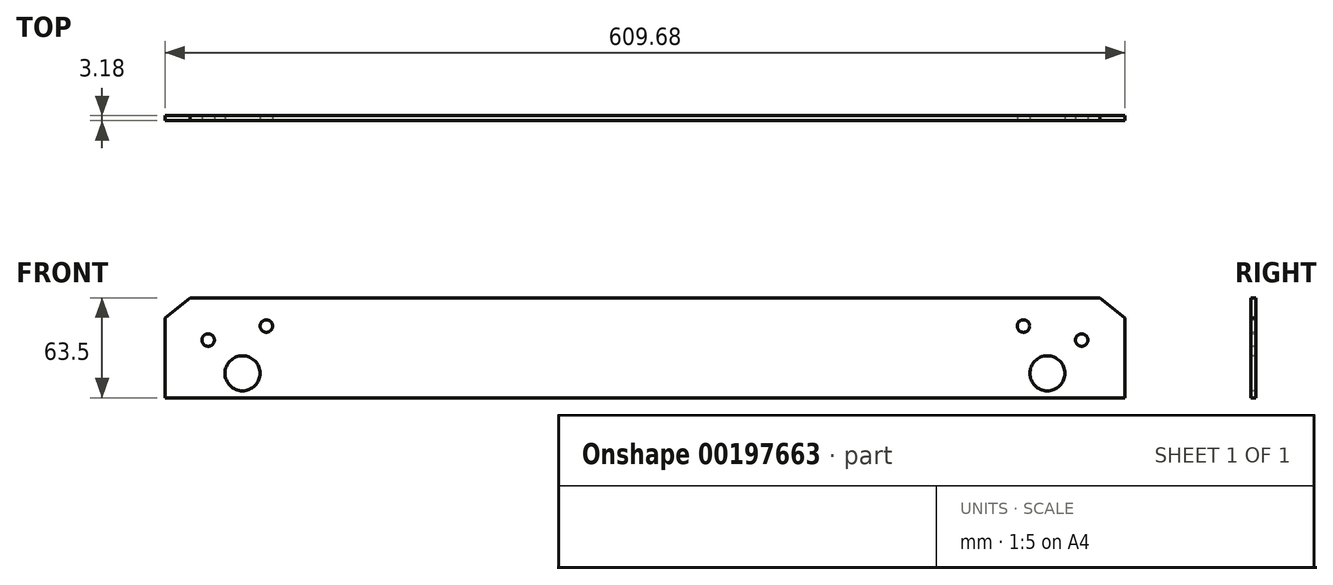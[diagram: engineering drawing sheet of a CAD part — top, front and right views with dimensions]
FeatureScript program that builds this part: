
annotation { "Feature Type Name" : "Feature", "Feature Type Description" : "" }
export const myFeature = defineFeature(function(context is Context, id is Id, definition is map)
    precondition{}
    {
        {
            var Q0;
            Q0=qCreatedBy(makeId("Front.planeOp"),FACE);
            var sketch = newSketch(context, id + "F0", { "sketchPlane" : qUnion([Q0])});
            skLineSegment(sketch, "E0.0", {"start": v(-467.1, 51.6) * mm, "end": v(110.76, 51.6) * mm});
            skCircle(sketch, "E1", {"center": v(99.23, 24.79) * mm, "radius": 3.96 * mm});
            skCircle(sketch, "E2", {"center": v(62.27, 33.68) * mm, "radius": 3.96 * mm});
            skCircle(sketch, "E3", {"center": v(77.43, 3.65) * mm, "radius": 11.11 * mm});
            skLineSegment(sketch, "E4.0", {"start": v(126.73, 38.9) * mm, "end": v(126.65, -11.9) * mm});
            skLineSegment(sketch, "E5.0", {"start": v(-482.87, 38.9) * mm, "end": v(-482.95, -11.9) * mm});
            skCircle(sketch, "E6.MirrorC", {"center": v(-455.56, 24.79) * mm, "radius": 3.96 * mm});
            skCircle(sketch, "E7.MirrorC", {"center": v(-418.6, 33.68) * mm, "radius": 3.96 * mm});
            skCircle(sketch, "E8.MirrorC", {"center": v(-433.77, 3.65) * mm, "radius": 11.11 * mm});
            skLineSegment(sketch, "E9", {"start": v(110.76, 51.6) * mm, "end": v(126.73, 38.9) * mm});
            skLineSegment(sketch, "E10", {"start": v(-467.1, 51.6) * mm, "end": v(-482.79, 38.9) * mm});
            skLineSegment(sketch, "E11", {"start": v(126.65, -11.9) * mm, "end": v(-482.95, -11.9) * mm});
            skSolve(sketch);
        }
        {
            var Q0;
            Q0=sQuery(id+"F0.wireOp",EDGE,"E0.0");
            var Q1;
            Q1=sQuery(id+"F0.wireOp",EDGE,"02333bd6-0d12-4fb4-9101-4d419dfe405c1.MirrorCS");
            var Q2;
            Q2=sQuery(id+"F0.wireOp",EDGE,"E5.0");
            var Q3;
            Q3=sQuery(id+"F0.wireOp",EDGE,"E4.0");
            var Q4;
            Q4=sQuery(id+"F0.wireOp",EDGE,"E9");
            var Q5;
            Q5=sQuery(id+"F0.wireOp",EDGE,"17ed3c64-61a1-4433-a5f3-46904ccfa39a0.MirrorCS");
            var Q6;
            Q6=sQuery(id+"F0.wireOp",EDGE,"E10");
            var Q7;
            Q7=sQuery(id+"F0.wireOp",EDGE,"E3");
            var Q8;
            Q8=sQuery(id+"F0.wireOp",EDGE,"E1");
            var Q9;
            Q9=sQuery(id+"F0.wireOp",EDGE,"E2");
            var Q10;
            Q10=sQuery(id+"F0.wireOp",EDGE,"E8.MirrorC");
            var Q11;
            Q11=sQuery(id+"F0.wireOp",EDGE,"E7.MirrorC");
            var Q12;
            Q12=sQuery(id+"F0.wireOp",EDGE,"E6.MirrorC");
            var Q13;
            Q13=sQuery(id+"F0.wireOp",EDGE,"E11");
            extrude(context, id + "F1", {"bodyType" : ToolBodyType.SURFACE, "surfaceEntities" : qUnion([Q0, Q1, Q2, Q3, Q4, Q5, Q6, Q7, Q8, Q9, Q10, Q11, Q12, Q13]), "depth" : 3.17 * mm});
        }
    });
